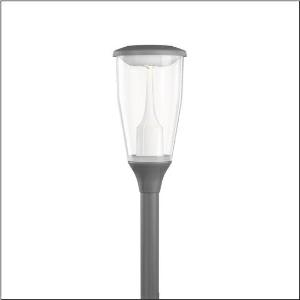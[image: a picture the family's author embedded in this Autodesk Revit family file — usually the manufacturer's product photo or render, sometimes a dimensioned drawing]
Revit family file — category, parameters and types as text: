
# Revit family: dl_11_iq___p1_0a_5xa5575bf14h000022_7e97
name_source: partatom
category: Lighting Fixtures
units: mm (PartAtom-declared; Revit-internal decimal feet)

## family parameters
Cut with Voids When Loaded = No
Host = Face
Light Source = No
Part Type = Normal
Room Calculation Point = No
Round Connector Dimension = Use Diameter
Shared = No

## types (1)
- --- (1 x LED, 1530 lm, 12.9 W, 2200K)
    Apparent Load = 13 VA
    CIE Flux Codes = 34 63 91 95 100
    Color Rendering = 70
    Color Temperature = 2200K
    Default Elevation = 1800 mm
    Description = DL 11 iQ, mast luminaire, Module 540 iQ-SR, primary light control with 3 zone facetted reflector, of plastic, silver coated, highly specular, structured, primary optical cover: cover, of PMMA, transparent, light distribution: P1.0a, light emission: direct distribution, primary light characteristic: asymmetric, installation type: post-top, LED, High Power LED, rated luminous flux: 1.560lm, luminous efficacy: 149lm/W, light colour: 722, colour temperature: 2200K, control: Street-Remote, Auto-Match, Temp-Guard, Lumen-Switch, Night-Set, Smart-Wire, Light-Fading, Desk-Remote (wireless, voltage-free reading and setting of iQ features in the workshop via application-optimized NFC function/RFID function), optimised constant luminous flux control (CLO 2.0), mains connection: 220..240V, AC, 50/60Hz, connection cable pre-assembled, cable length: 5,5m, wiring characteristics: H07RN-F, 5-core, 1.5mm², start of lifetime: 13W, end of service life: 13W, reduction: 5W, luminaire housing, upper part, of diecast aluminium, coated, Siteco® metallic grey (DB 702S), spigot size: 76mm (post-top), post-top mast mounting element, of diecast aluminium, coated, Siteco® metallic grey (DB 702S), Module 540 iQ-SR, traffic white (RAL 9016), equipment: standard, protection rating (complete): IP66, insulation class (complete): insulation class II (safety insulation), certification: CE, ENEC, ENEC+, VDE, packaging unit: 1 piece

Light Distribution: P1.0a
    Height = 665 mm
    Lamp = 1 x LED
    Lamp Light Flux = 1530 lm
    Lamp Power = 12.9 W
    Lamp count = 1
    Length = 334 mm
    Luminous efficacy = 119 lm/W
    Manufacturer = Siteco
    ModVariant = No
    Model = 5XA5575BF14H000022
    Number of Poles = 1
    OnlyDefault = Yes
    Power Factor = 1
    Product Name = DL 11 iQ | P1.0a
    Product group = mast luminaire | pylon top
    ProductGroupID = 6100
    Protection Class = Protection class II
    Protection Degree = IP 66
    RLX_Detail_Level = 1
    RLX_Emergency_Light_Flux = 0 lm
    RLX_Emergency_Type = 0
    RLX_Emergency_Type_DB = No
    RlxData = <blob elided: 103681 chars, md5=955da0f6>
    Socket = socket
    Standby Power = 0 W
    System Light Flux = 1530 lm
    System Power = 13 W
    Type Comments = factory setting: luminous flux: 100 % | dim-lin: 254 | 516 mA
    Type Image = l_1258354.jpg
    URL = http://relux.com
    VarID = @adj_042339
    Voltage = 0 V
    Weight = 0.00 kg
    Width = 0 mm  [stored 0 ft]

note: [stored X ft] marks values corroborated as IEEE doubles in the binary element streams (Revit-internal decimal feet)

## geometry (parser evidence)
native form markers: Blend x4, Sweep x12
no freeform markers — native parametric forms only
